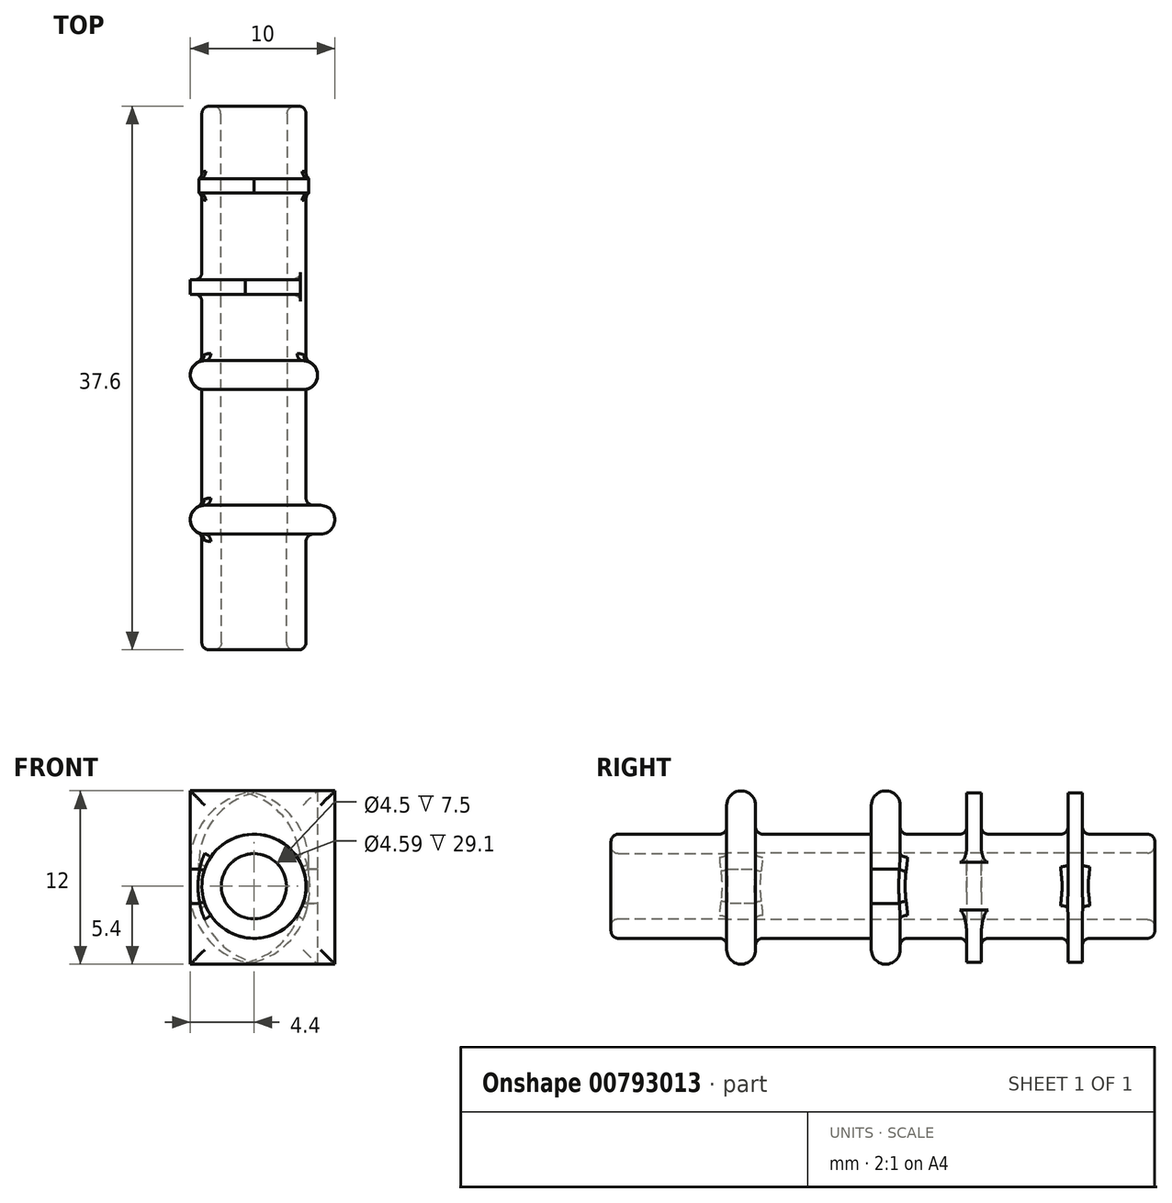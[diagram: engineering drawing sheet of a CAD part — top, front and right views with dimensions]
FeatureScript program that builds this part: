
annotation { "Feature Type Name" : "Feature", "Feature Type Description" : "" }
export const myFeature = defineFeature(function(context is Context, id is Id, definition is map)
    precondition{}
    {
        {
            var Q0;
            Q0=qCreatedBy(makeId("Front.planeOp"),FACE);
            var sketch = newSketch(context, id + "F0", { "sketchPlane" : qUnion([Q0])});
            skCircle(sketch, "E0", {"center": v(0, -3.6) * mm, "radius": 3.6 * mm});
            skCircle(sketch, "E1", {"center": v(0, -3.6) * mm, "radius": 2.25 * mm});
            skSolve(sketch);
        }
        {
            var Q0;
            Q0 = qSketchRegion(id + "F0", true);
            extrude(context, id + "F1", {"entities" : qUnion([Q0]), "depth" : 37.6 * mm, "offsetDistance" : 25 * mm});
        }
        {
            var Q0;
            Q0=qCreatedBy(makeId("Top.planeOp"),FACE);
            var sketch = newSketch(context, id + "F2", { "sketchPlane" : qUnion([Q0])});
            skLineSegment(sketch, "E2.bottom", {"start": v(-3.8, -6) * mm, "end": v(3.8, -6) * mm});
            skLineSegment(sketch, "E2.top", {"start": v(-3.8, -5) * mm, "end": v(3.8, -5) * mm});
            skLineSegment(sketch, "E2.left", {"start": v(-3.8, -6) * mm, "end": v(-3.8, -5) * mm});
            skLineSegment(sketch, "E2.right", {"start": v(3.8, -6) * mm, "end": v(3.8, -5) * mm});
            skPoint(sketch, "E2.middle", {"position": v(0, -5.5) * mm});
            skLineSegment(sketch, "E3.bottom", {"start": v(-4.4, -13) * mm, "end": v(3.2, -13) * mm});
            skLineSegment(sketch, "E3.top", {"start": v(-4.4, -12) * mm, "end": v(3.2, -12) * mm});
            skLineSegment(sketch, "E3.left", {"start": v(-4.4, -13) * mm, "end": v(-4.4, -12) * mm});
            skLineSegment(sketch, "E3.right", {"start": v(3.2, -13) * mm, "end": v(3.2, -12) * mm});
            skPoint(sketch, "E3.middle", {"position": v(0, -12.5) * mm});
            skLineSegment(sketch, "E4.bottom", {"start": v(-4.4, -19.6) * mm, "end": v(4.4, -19.6) * mm});
            skLineSegment(sketch, "E4.top", {"start": v(-4.4, -17.6) * mm, "end": v(4.4, -17.6) * mm});
            skLineSegment(sketch, "E4.left", {"start": v(-4.4, -19.6) * mm, "end": v(-4.4, -17.6) * mm});
            skLineSegment(sketch, "E4.right", {"start": v(4.4, -19.6) * mm, "end": v(4.4, -17.6) * mm});
            skPoint(sketch, "E4.middle", {"position": v(0, -18.6) * mm});
            skLineSegment(sketch, "E5.bottom", {"start": v(-4.4, -27.6) * mm, "end": v(5.6, -27.6) * mm});
            skLineSegment(sketch, "E5.top", {"start": v(-4.4, -29.6) * mm, "end": v(5.6, -29.6) * mm});
            skLineSegment(sketch, "E5.left", {"start": v(-4.4, -27.6) * mm, "end": v(-4.4, -29.6) * mm});
            skLineSegment(sketch, "E5.right", {"start": v(5.6, -27.6) * mm, "end": v(5.6, -29.6) * mm});
            skPoint(sketch, "E5.middle", {"position": v(0, -28.6) * mm});
            skSolve(sketch);
        }
        {
            var Q0;
            Q0 = qSketchRegion(id + "F2", true);
            extrude(context, id + "F3", {"entities" : qUnion([Q0]), "operationType" : NewBodyOperationType.ADD, "oppositeDirection" : true, "depth" : 9 * mm, "offsetDistance" : 25 * mm, "hasSecondDirection" : true, "secondDirectionOppositeDirection" : false, "secondDirectionDepth" : 3 * mm});
        }
        {
            var Q0;
            Q0=makeQuery(id+"F3.opExtrude","SWEPT_EDGE",EDGE,{"disambiguationData":[OSD([sQuery(id+"F2.wireOp",EDGE,"E5.top"),sQuery(id+"F2.wireOp",EDGE,"E5.right")])]});
            var Q1;
            Q1=makeQuery(id+"F3.opExtrude","SWEPT_EDGE",EDGE,{"disambiguationData":[OSD([sQuery(id+"F2.wireOp",EDGE,"E5.bottom"),sQuery(id+"F2.wireOp",EDGE,"E5.right")])]});
            var Q2;
            Q2=makeQuery(id+"F3.opExtrude","CAP_EDGE",EDGE,{"disambiguationData":[OSD([sQuery(id+"F2.wireOp",EDGE,"E5.top")])],"isStart":true});
            var Q3;
            Q3=makeQuery(id+"F3.opExtrude","SWEPT_EDGE",EDGE,{"disambiguationData":[OSD([sQuery(id+"F2.wireOp",EDGE,"E5.top"),sQuery(id+"F2.wireOp",EDGE,"E5.left")])]});
            var Q4;
            Q4=makeQuery(id+"F3.opExtrude","CAP_EDGE",EDGE,{"disambiguationData":[OSD([sQuery(id+"F2.wireOp",EDGE,"E5.top")])],"isStart":false});
            var Q5;
            Q5=makeQuery(id+"F3.opExtrude","CAP_EDGE",EDGE,{"disambiguationData":[OSD([sQuery(id+"F2.wireOp",EDGE,"E5.bottom")])],"isStart":true});
            var Q6;
            Q6=makeQuery(id+"F3.opExtrude","SWEPT_EDGE",EDGE,{"disambiguationData":[OSD([sQuery(id+"F2.wireOp",EDGE,"E5.bottom"),sQuery(id+"F2.wireOp",EDGE,"E5.left")])]});
            var Q7;
            Q7=makeQuery(id+"F3.opExtrude","CAP_EDGE",EDGE,{"disambiguationData":[OSD([sQuery(id+"F2.wireOp",EDGE,"E5.bottom")])],"isStart":false});
            var Q8;
            Q8=makeQuery(id+"F3.opExtrude","SWEPT_EDGE",EDGE,{"disambiguationData":[OSD([sQuery(id+"F2.wireOp",EDGE,"E4.bottom"),sQuery(id+"F2.wireOp",EDGE,"E4.left")])]});
            var Q9;
            Q9=makeQuery(id+"F3.opExtrude","SWEPT_EDGE",EDGE,{"disambiguationData":[OSD([sQuery(id+"F2.wireOp",EDGE,"E4.top"),sQuery(id+"F2.wireOp",EDGE,"E4.left")])]});
            var Q10;
            Q10=makeQuery(id+"F3.opExtrude","CAP_EDGE",EDGE,{"disambiguationData":[OSD([sQuery(id+"F2.wireOp",EDGE,"E4.top")])],"isStart":true});
            var Q11;
            Q11=makeQuery(id+"F3.opExtrude","SWEPT_EDGE",EDGE,{"disambiguationData":[OSD([sQuery(id+"F2.wireOp",EDGE,"E4.bottom"),sQuery(id+"F2.wireOp",EDGE,"E4.right")])]});
            var Q12;
            Q12=makeQuery(id+"F3.opExtrude","CAP_EDGE",EDGE,{"disambiguationData":[OSD([sQuery(id+"F2.wireOp",EDGE,"E4.bottom")])],"isStart":true});
            var Q13;
            Q13=makeQuery(id+"F3.opExtrude","SWEPT_EDGE",EDGE,{"disambiguationData":[OSD([sQuery(id+"F2.wireOp",EDGE,"E4.top"),sQuery(id+"F2.wireOp",EDGE,"E4.right")])]});
            var Q14;
            Q14=makeQuery(id+"F3.opExtrude","CAP_EDGE",EDGE,{"disambiguationData":[OSD([sQuery(id+"F2.wireOp",EDGE,"E4.top")])],"isStart":false});
            var Q15;
            Q15=makeQuery(id+"F3.opExtrude","CAP_EDGE",EDGE,{"disambiguationData":[OSD([sQuery(id+"F2.wireOp",EDGE,"E4.bottom")])],"isStart":false});
            fillet(context, id + "F4", {"entities" : qUnion([Q0, Q1, Q2, Q3, Q4, Q5, Q6, Q7, Q8, Q9, Q10, Q11, Q12, Q13, Q14, Q15]), "radius" : 1 * mm, "tangentPropagation" : true, "allowEdgeOverflow" : false});
        }
        {
            var Q0;
            Q0=makeQuery(id+"F3.boolean.opBoolean","SPLIT",FACE,{"disambiguationData":[TD([makeQuery(id+"F1.opExtrude","SWEPT_FACE",FACE,{"disambiguationData":[OSD([sQuery(id+"F0.wireOp",EDGE,"E1")])]})])],"derivedFrom":makeQuery(id+"F3.opExtrude","SWEPT_FACE",FACE,{"disambiguationData":[OSD([sQuery(id+"F2.wireOp",EDGE,"E5.top")])]})});
            var sketch = newSketch(context, id + "F5", { "sketchPlane" : qUnion([Q0])});
            skCircle(sketch, "E6", {"center": v(0, -3.6) * mm, "radius": 2.3 * mm});
            skSolve(sketch);
        }
        {
            var Q0;
            Q0 = qSketchRegion(id + "F5", true);
            extrude(context, id + "F6", {"entities" : qUnion([Q0]), "operationType" : NewBodyOperationType.REMOVE, "endBound" : BoundingType.THROUGH_ALL, "oppositeDirection" : true, "depth" : 25 * mm, "offsetDistance" : 25 * mm});
        }
        {
            var Q0;
            Q0=makeQuery(id+"F3.boolean.opBoolean","INTERSECT",EDGE,{"derivedFrom":[makeQuery(id+"F1.opExtrude","SWEPT_FACE",FACE,{"disambiguationData":[OSD([sQuery(id+"F0.wireOp",EDGE,"E0")])]}),makeQuery(id+"F3.opExtrude","SWEPT_FACE",FACE,{"disambiguationData":[OSD([sQuery(id+"F2.wireOp",EDGE,"E4.top")])]})]});
            var Q1;
            Q1=makeQuery(id+"F3.boolean.opBoolean","INTERSECT",EDGE,{"derivedFrom":[makeQuery(id+"F1.opExtrude","SWEPT_FACE",FACE,{"disambiguationData":[OSD([sQuery(id+"F0.wireOp",EDGE,"E0")])]}),makeQuery(id+"F3.opExtrude","SWEPT_FACE",FACE,{"disambiguationData":[OSD([sQuery(id+"F2.wireOp",EDGE,"E3.bottom")])]})]});
            var Q2;
            Q2=makeQuery(id+"F3.boolean.opBoolean","INTERSECT",EDGE,{"derivedFrom":[makeQuery(id+"F1.opExtrude","SWEPT_FACE",FACE,{"disambiguationData":[OSD([sQuery(id+"F0.wireOp",EDGE,"E0")])]}),makeQuery(id+"F3.opExtrude","SWEPT_FACE",FACE,{"disambiguationData":[OSD([sQuery(id+"F2.wireOp",EDGE,"E3.top")])]})]});
            var Q3;
            Q3=makeQuery(id+"F3.boolean.opBoolean","INTERSECT",EDGE,{"derivedFrom":[makeQuery(id+"F1.opExtrude","SWEPT_FACE",FACE,{"disambiguationData":[OSD([sQuery(id+"F0.wireOp",EDGE,"E0")])]}),makeQuery(id+"F3.opExtrude","SWEPT_FACE",FACE,{"disambiguationData":[OSD([sQuery(id+"F2.wireOp",EDGE,"E2.top")])]})]});
            var Q4;
            Q4=makeQuery(id+"F3.boolean.opBoolean","INTERSECT",EDGE,{"derivedFrom":[makeQuery(id+"F1.opExtrude","SWEPT_FACE",FACE,{"disambiguationData":[OSD([sQuery(id+"F0.wireOp",EDGE,"E0")])]}),makeQuery(id+"F3.opExtrude","SWEPT_FACE",FACE,{"disambiguationData":[OSD([sQuery(id+"F2.wireOp",EDGE,"E2.bottom")])]})]});
            var Q5;
            Q5=makeQuery(id+"F1.opExtrude","CAP_EDGE",EDGE,{"disambiguationData":[OSD([sQuery(id+"F0.wireOp",EDGE,"E0")])],"isStart":true});
            var Q6;
            Q6=makeQuery(id+"F6.boolean.opBoolean","INTERSECT",EDGE,{"derivedFrom":[makeQuery(id+"F1.opExtrude","CAP_FACE",FACE,{"disambiguationData":[OSD([sQuery(id+"F0.wireOp",EDGE,"E0"),sQuery(id+"F0.wireOp",EDGE,"E1")])],"isStart":true}),makeQuery(id+"F6.opExtrude","SWEPT_FACE",FACE,{"disambiguationData":[OSD([sQuery(id+"F5.wireOp",EDGE,"E6")])]})]});
            var Q7;
            Q7=makeQuery(id+"F3.boolean.opBoolean","INTERSECT",EDGE,{"derivedFrom":[makeQuery(id+"F1.opExtrude","SWEPT_FACE",FACE,{"disambiguationData":[OSD([sQuery(id+"F0.wireOp",EDGE,"E0")])]}),makeQuery(id+"F3.opExtrude","SWEPT_FACE",FACE,{"disambiguationData":[OSD([sQuery(id+"F2.wireOp",EDGE,"E5.top")])]})]});
            var Q8;
            Q8=makeQuery(id+"F1.opExtrude","CAP_EDGE",EDGE,{"disambiguationData":[OSD([sQuery(id+"F0.wireOp",EDGE,"E1")])],"isStart":false});
            var Q9;
            Q9=makeQuery(id+"F1.opExtrude","CAP_EDGE",EDGE,{"disambiguationData":[OSD([sQuery(id+"F0.wireOp",EDGE,"E0")])],"isStart":false});
            var Q10;
            Q10=makeQuery(id+"F3.boolean.opBoolean","INTERSECT",EDGE,{"derivedFrom":[makeQuery(id+"F1.opExtrude","SWEPT_FACE",FACE,{"disambiguationData":[OSD([sQuery(id+"F0.wireOp",EDGE,"E0")])]}),makeQuery(id+"F3.opExtrude","SWEPT_FACE",FACE,{"disambiguationData":[OSD([sQuery(id+"F2.wireOp",EDGE,"E5.bottom")])]})]});
            fillet(context, id + "F7", {"entities" : qUnion([Q0, Q1, Q2, Q3, Q4, Q5, Q6, Q7, Q8, Q9, Q10]), "radius" : 0.5 * mm, "tangentPropagation" : true, "allowEdgeOverflow" : false});
        }
        {
            var Q0;
            Q0=makeQuery(id+"F3.opExtrude","CAP_EDGE",EDGE,{"disambiguationData":[OSD([sQuery(id+"F2.wireOp",EDGE,"E3.right")])],"isStart":true});
            var Q1;
            Q1=makeQuery(id+"F3.opExtrude","CAP_EDGE",EDGE,{"disambiguationData":[OSD([sQuery(id+"F2.wireOp",EDGE,"E3.left")])],"isStart":true});
            var Q2;
            Q2=makeQuery(id+"F3.opExtrude","CAP_EDGE",EDGE,{"disambiguationData":[OSD([sQuery(id+"F2.wireOp",EDGE,"E3.left")])],"isStart":false});
            var Q3;
            Q3=makeQuery(id+"F3.opExtrude","CAP_EDGE",EDGE,{"disambiguationData":[OSD([sQuery(id+"F2.wireOp",EDGE,"E3.right")])],"isStart":false});
            var Q4;
            Q4=makeQuery(id+"F3.opExtrude","CAP_EDGE",EDGE,{"disambiguationData":[OSD([sQuery(id+"F2.wireOp",EDGE,"E2.right")])],"isStart":false});
            var Q5;
            Q5=makeQuery(id+"F3.opExtrude","CAP_EDGE",EDGE,{"disambiguationData":[OSD([sQuery(id+"F2.wireOp",EDGE,"E2.left")])],"isStart":false});
            var Q6;
            Q6=makeQuery(id+"F3.opExtrude","CAP_EDGE",EDGE,{"disambiguationData":[OSD([sQuery(id+"F2.wireOp",EDGE,"E2.left")])],"isStart":true});
            var Q7;
            Q7=makeQuery(id+"F3.opExtrude","CAP_EDGE",EDGE,{"disambiguationData":[OSD([sQuery(id+"F2.wireOp",EDGE,"E2.right")])],"isStart":true});
            fillet(context, id + "F8", {"entities" : qUnion([Q0, Q1, Q2, Q3, Q4, Q5, Q6, Q7]), "radius" : 5 * mm, "tangentPropagation" : true, "allowEdgeOverflow" : false});
        }
    });
